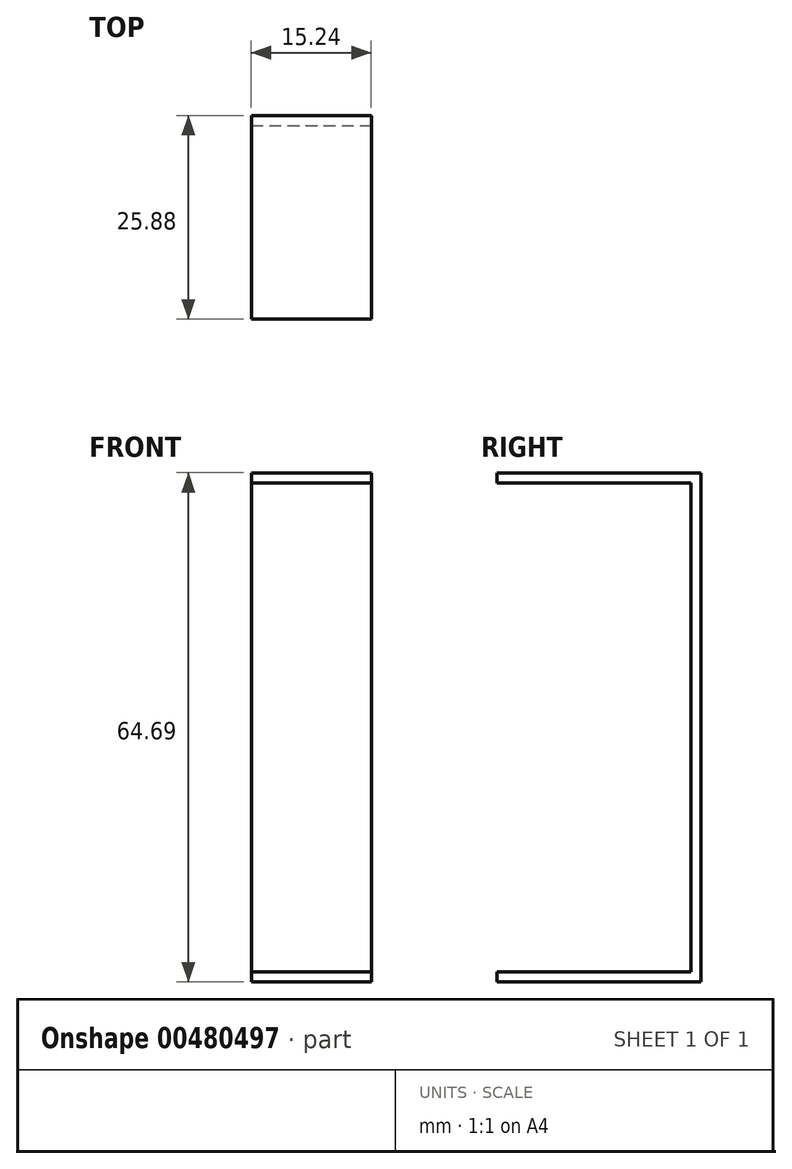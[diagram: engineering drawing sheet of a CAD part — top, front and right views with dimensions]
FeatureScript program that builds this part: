
annotation { "Feature Type Name" : "Feature", "Feature Type Description" : "" }
export const myFeature = defineFeature(function(context is Context, id is Id, definition is map)
    precondition{}
    {
        {
            var Q0;
            Q0=qCreatedBy(makeId("Front.planeOp"),FACE);
            var sketch = newSketch(context, id + "F0", { "sketchPlane" : qUnion([Q0])});
            skLineSegment(sketch, "E0.bottom", {"start": v(-8.17, 31.32) * mm, "end": v(7.07, 31.32) * mm});
            skLineSegment(sketch, "E0.top", {"start": v(-8.17, -33.37) * mm, "end": v(7.07, -33.37) * mm});
            skLineSegment(sketch, "E0.left", {"start": v(-8.17, 31.32) * mm, "end": v(-8.17, -33.37) * mm});
            skLineSegment(sketch, "E0.right", {"start": v(7.07, 31.32) * mm, "end": v(7.07, -33.37) * mm});
            skSolve(sketch);
        }
        {
            var Q0;
            Q0 = qSketchRegion(id + "F0", true);
            extrude(context, id + "F1", {"entities" : qUnion([Q0]), "depth" : 1.27 * mm});
        }
        {
            var Q0;
            Q0=makeQuery(id+"F1.opExtrude","SWEPT_FACE",FACE,{"disambiguationData":[OSD([sQuery(id+"F0.wireOp",EDGE,"E0.bottom")])]});
            var sketch = newSketch(context, id + "F2", { "sketchPlane" : qUnion([Q0])});
            skLineSegment(sketch, "E1", {"start": v(7.07, -1.27) * mm, "end": v(7.07, -25.88) * mm});
            skLineSegment(sketch, "E2", {"start": v(-8.17, -1.27) * mm, "end": v(-8.17, -25.88) * mm});
            skLineSegment(sketch, "E3", {"start": v(-8.17, -25.88) * mm, "end": v(7.07, -25.88) * mm});
            skSolve(sketch);
        }
        {
            var Q0;
            Q0=makeQuery(id+"F2.imprint","IMPRINT",FACE,{"disambiguationData":[TD([[makeQuery(id+"F2.imprint","IMPRINT",EDGE,{"derivedFrom":sQuery(id+"F2.wireOp",EDGE,"E1")}),-1.0]])]});
            extrude(context, id + "F3", {"entities" : qUnion([Q0]), "operationType" : NewBodyOperationType.ADD, "depth" : -1.27 * mm});
        }
        {
            var Q0;
            Q0=makeQuery(id+"F1.opExtrude","SWEPT_FACE",FACE,{"disambiguationData":[OSD([sQuery(id+"F0.wireOp",EDGE,"E0.top")])]});
            var sketch = newSketch(context, id + "F4", { "sketchPlane" : qUnion([Q0])});
            skLineSegment(sketch, "E4.bottom", {"start": v(-8.17, 1.27) * mm, "end": v(7.07, 1.27) * mm});
            skLineSegment(sketch, "E4.top", {"start": v(-8.17, 25.88) * mm, "end": v(7.07, 25.88) * mm});
            skLineSegment(sketch, "E4.left", {"start": v(-8.17, 1.27) * mm, "end": v(-8.17, 25.88) * mm});
            skLineSegment(sketch, "E4.right", {"start": v(7.07, 1.27) * mm, "end": v(7.07, 25.88) * mm});
            skSolve(sketch);
        }
        {
            var Q0;
            Q0=makeQuery(id+"F4.imprint","IMPRINT",FACE,{"disambiguationData":[TD([[makeQuery(id+"F4.imprint","IMPRINT",EDGE,{"derivedFrom":sQuery(id+"F4.wireOp",EDGE,"E4.bottom")}),1.0]])]});
            extrude(context, id + "F5", {"entities" : qUnion([Q0]), "operationType" : NewBodyOperationType.ADD, "depth" : -1.27 * mm});
        }
    });
